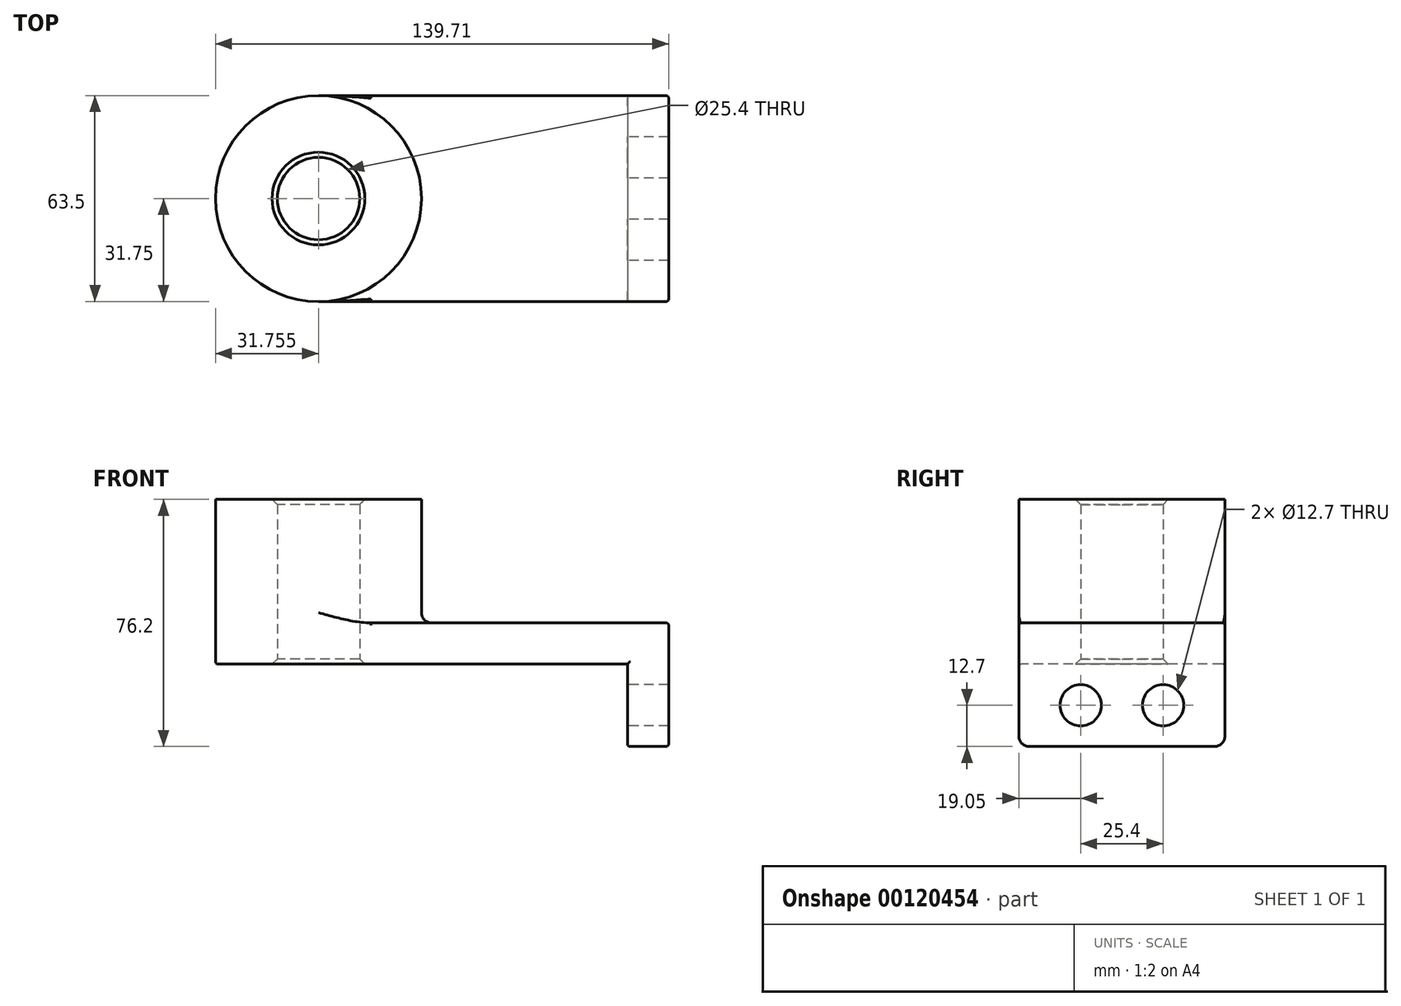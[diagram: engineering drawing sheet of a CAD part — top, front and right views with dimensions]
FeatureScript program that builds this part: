
annotation { "Feature Type Name" : "Feature", "Feature Type Description" : "" }
export const myFeature = defineFeature(function(context is Context, id is Id, definition is map)
    precondition{}
    {
        {
            var Q0;
            Q0=qCreatedBy(makeId("Top.planeOp"),FACE);
            var sketch = newSketch(context, id + "F0", { "sketchPlane" : qUnion([Q0])});
            skLineSegment(sketch, "E0.rect.bottom", {"start": v(-47.63, 31.75) * mm, "end": v(47.62, 31.75) * mm});
            skLineSegment(sketch, "E0.rect.top", {"start": v(-47.63, -31.75) * mm, "end": v(47.62, -31.75) * mm});
            skLineSegment(sketch, "E0.rect.left", {"start": v(-47.62, 31.75) * mm, "end": v(-47.63, -31.75) * mm});
            skLineSegment(sketch, "E0.rect.right", {"start": v(47.63, 31.75) * mm, "end": v(47.62, -31.75) * mm});
            skPoint(sketch, "E0.rect.middle", {"position": v(0, 0) * mm});
            skCircle(sketch, "E1", {"center": v(-47.62, 0) * mm, "radius": 31.75 * mm});
            skCircle(sketch, "E2", {"center": v(-47.62, 0) * mm, "radius": 12.7 * mm});
            skSolve(sketch);
        }
        {
            var Q0;
            Q0=qSketchRegion(id+"F0",true);
            extrude(context, id + "F1", {"entities" : qUnion([Q0]), "depth" : 12.7 * mm});
        }
        {
            var Q0;
            {var subQ0=sQuery(id+"F0.wireOp",EDGE,"E2");var subQ1=sQuery(id+"F0.wireOp",EDGE,"E0.rect.left");var subQ3=makeQuery(id+"F0.imprint","INTERSECT",VERTEX,{"disambiguationData":[OD(0.0)],"derivedFrom":[subQ1,subQ0]});Q0=makeQuery(id+"F0.imprint","IMPRINT",FACE,{"disambiguationData":[TD([[makeQuery(id+"F0.imprint","IMPRINT",EDGE,{"disambiguationData":[TD([[subQ3,-1.0]])],"derivedFrom":subQ0}),-1.0]])]});}
            var Q1;
            {var subQ0=sQuery(id+"F0.wireOp",EDGE,"E2");var subQ1=sQuery(id+"F0.wireOp",EDGE,"E0.rect.left");var subQ3=makeQuery(id+"F0.imprint","INTERSECT",VERTEX,{"disambiguationData":[OD(0.0)],"derivedFrom":[subQ1,subQ0]});Q1=makeQuery(id+"F0.imprint","IMPRINT",FACE,{"disambiguationData":[TD([[makeQuery(id+"F0.imprint","IMPRINT",EDGE,{"disambiguationData":[TD([[subQ3,1.0]])],"derivedFrom":subQ0}),-1.0]])]});}
            extrude(context, id + "F2", {"entities" : qUnion([Q0, Q1]), "operationType" : NewBodyOperationType.ADD, "depth" : 50.8 * mm});
        }
        {
            var Q0;
            Q0=makeQuery(id+"F1.opExtrude","SWEPT_FACE",FACE,{"disambiguationData":[OSD([sQuery(id+"F0.wireOp",EDGE,"E0.rect.right")])]});
            var sketch = newSketch(context, id + "F3", { "sketchPlane" : qUnion([Q0])});
            skLineSegment(sketch, "E3.bottom", {"start": v(31.75, 12.7) * mm, "end": v(-31.75, 12.7) * mm});
            skLineSegment(sketch, "E3.top", {"start": v(31.75, -25.4) * mm, "end": v(-31.75, -25.4) * mm});
            skLineSegment(sketch, "E3.left", {"start": v(31.75, 12.7) * mm, "end": v(31.75, -25.4) * mm});
            skLineSegment(sketch, "E3.right", {"start": v(-31.75, 12.7) * mm, "end": v(-31.75, -25.4) * mm});
            skCircle(sketch, "E4", {"center": v(-12.7, -12.7) * mm, "radius": 6.35 * mm});
            skLineSegment(sketch, "E5", {"start": v(0, 0) * mm, "end": v(0, -25.4) * mm, "construction": true});
            skCircle(sketch, "E6.MirrorC", {"center": v(12.7, -12.7) * mm, "radius": 6.35 * mm});
            skSolve(sketch);
        }
        {
            var Q0;
            {var subQ2=sQuery(id+"F3.wireOp",EDGE,"E3.bottom");Q0=makeQuery(id+"F3.imprint","IMPRINT",FACE,{"disambiguationData":[TD([[makeQuery(id+"F3.imprint","IMPRINT",EDGE,{"derivedFrom":subQ2}),1.0]])]});}
            var Q1;
            {var subQ2=sQuery(id+"F3.wireOp",EDGE,"E3.top");Q1=makeQuery(id+"F3.imprint","IMPRINT",FACE,{"disambiguationData":[TD([[makeQuery(id+"F3.imprint","IMPRINT",EDGE,{"derivedFrom":subQ2}),-1.0]])]});}
            extrude(context, id + "F4", {"entities" : qUnion([Q0, Q1]), "operationType" : NewBodyOperationType.ADD, "depth" : 12.7 * mm});
        }
        {
            var Q0;
            {var subQ0=sQuery(id+"F0.wireOp",EDGE,"E1");Q0=makeQuery(id+"F2.boolean.opBoolean","INTERSECT",EDGE,{"derivedFrom":[makeQuery(id+"F1.opExtrude","CAP_FACE",FACE,{"disambiguationData":[OSD([sQuery(id+"F0.wireOp",EDGE,"E0.rect.bottom"),sQuery(id+"F0.wireOp",EDGE,"E0.rect.top"),sQuery(id+"F0.wireOp",EDGE,"E0.rect.right"),subQ0,sQuery(id+"F0.wireOp",EDGE,"E2")])],"isStart":false}),makeQuery(id+"F2.opExtrude","SWEPT_FACE",FACE,{"disambiguationData":[OSD([subQ0])]})]});}
            var Q1;
            Q1=makeQuery(id+"F4.opExtrude","SWEPT_EDGE",EDGE,{"disambiguationData":[OSD([sQuery(id+"F3.wireOp",EDGE,"E3.top"),sQuery(id+"F3.wireOp",EDGE,"E3.right")])]});
            var Q2;
            Q2=makeQuery(id+"F4.opExtrude","SWEPT_EDGE",EDGE,{"disambiguationData":[OSD([sQuery(id+"F3.wireOp",EDGE,"E3.top"),sQuery(id+"F3.wireOp",EDGE,"E3.left")])]});
            fillet(context, id + "F5", {"entities" : qUnion([Q0, Q1, Q2]), "radius" : 3.17 * mm, "tangentPropagation" : true, "allowEdgeOverflow" : false});
        }
        {
            var Q0;
            Q0=makeQuery(id+"F4.boolean.opBoolean","MERGE",EDGE,{"derivedFrom":[makeQuery(id+"F1.opExtrude","CAP_EDGE",EDGE,{"disambiguationData":[OSD([sQuery(id+"F0.wireOp",EDGE,"E0.rect.top")])],"isStart":false}),makeQuery(id+"F4.opExtrude","SWEPT_EDGE",EDGE,{"disambiguationData":[OSD([sQuery(id+"F3.wireOp",EDGE,"E3.bottom"),sQuery(id+"F3.wireOp",EDGE,"E3.right")])]})]});
            var Q1;
            Q1=makeQuery(id+"F4.opExtrude","CAP_EDGE",EDGE,{"disambiguationData":[OSD([sQuery(id+"F3.wireOp",EDGE,"E3.right")])],"isStart":false});
            var Q2;
            Q2=makeQuery(id+"F4.opExtrude","CAP_EDGE",EDGE,{"disambiguationData":[OSD([sQuery(id+"F3.wireOp",EDGE,"E3.bottom")])],"isStart":false});
            var Q3;
            Q3=makeQuery(id+"F4.boolean.opBoolean","MERGE",EDGE,{"derivedFrom":[makeQuery(id+"F1.opExtrude","CAP_EDGE",EDGE,{"disambiguationData":[OSD([sQuery(id+"F0.wireOp",EDGE,"E0.rect.bottom")])],"isStart":false}),makeQuery(id+"F4.opExtrude","SWEPT_EDGE",EDGE,{"disambiguationData":[OSD([sQuery(id+"F3.wireOp",EDGE,"E3.bottom"),sQuery(id+"F3.wireOp",EDGE,"E3.left")])]})]});
            var Q4;
            Q4=makeQuery(id+"F1.opExtrude","CAP_EDGE",EDGE,{"disambiguationData":[OSD([sQuery(id+"F0.wireOp",EDGE,"E0.rect.top")])],"isStart":true});
            var Q5;
            Q5=makeQuery(id+"F4.opExtrude","CAP_EDGE",EDGE,{"disambiguationData":[OSD([sQuery(id+"F3.wireOp",EDGE,"E3.right")])],"isStart":true});
            fillet(context, id + "F6", {"entities" : qUnion([Q0, Q1, Q2, Q3, Q4, Q5]), "radius" : 0.79 * mm, "tangentPropagation" : true, "allowEdgeOverflow" : false});
        }
        {
            var Q0;
            {var subQ0=sQuery(id+"F0.wireOp",EDGE,"E2");Q0=makeQuery(id+"F2.boolean.opBoolean","MERGE",FACE,{"derivedFrom":[makeQuery(id+"F1.opExtrude","SWEPT_FACE",FACE,{"disambiguationData":[OSD([subQ0])]}),makeQuery(id+"F2.opExtrude","SWEPT_FACE",FACE,{"disambiguationData":[OSD([subQ0])]})]});}
            chamfer(context, id + "F7", {"entities" : qUnion([Q0]), "width" : 1.6 * mm, "tangentPropagation" : true});
        }
    });
